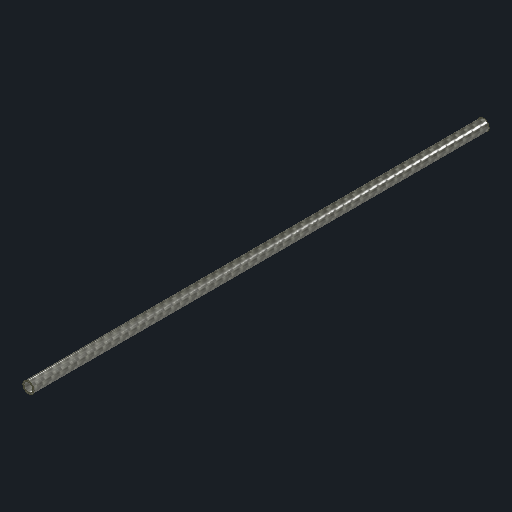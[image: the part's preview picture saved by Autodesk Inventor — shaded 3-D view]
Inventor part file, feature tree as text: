
AUTODESK INVENTOR PART (.ipt)
format: ipt  version: 2024.1 (Build 281209000, 209)  size: 198,144 bytes
history: native  units: mm
features: extrude x1
ambient origin geometry x8: Origin, YZ Plane, XZ Plane, XY Plane, X Axis, Y Axis, Z Axis, Center Point
bodies: Solid1 (feature_tree)
feature tree (1):
  extrude  "Extrusion1"  Depth=10.0mm
